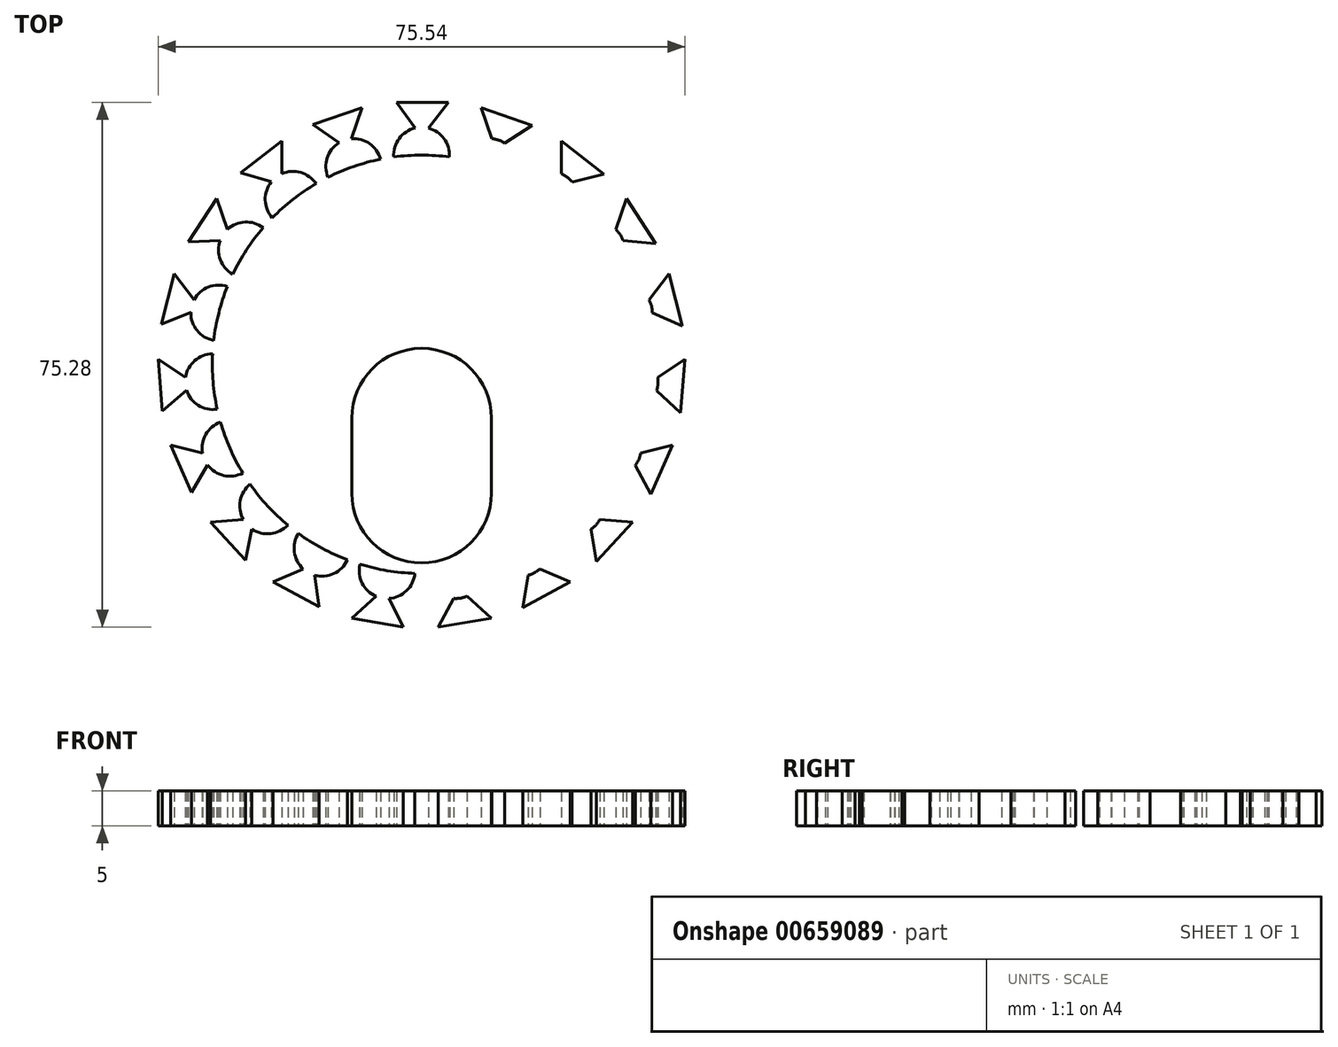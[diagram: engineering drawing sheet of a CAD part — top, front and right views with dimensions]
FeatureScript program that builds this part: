
annotation { "Feature Type Name" : "Feature", "Feature Type Description" : "" }
export const myFeature = defineFeature(function(context is Context, id is Id, definition is map)
    precondition{}
    {
        {
            var Q0;
            Q0=qCreatedBy(makeId("Top.planeOp"),FACE);
            var sketch = newSketch(context, id + "F0", { "sketchPlane" : qUnion([Q0])});
            skPoint(sketch, "E0.center", {"position": v(0, 0) * mm});
            skCircle(sketch, "E1", {"center": v(0, 0) * mm, "radius": 30 * mm});
            skArc(sketch, "E2", {"start": v(4, 29.73) * mm, "mid": v(0, 34) * mm, "end": v(-4, 29.73) * mm});
            skLineSegment(sketch, "E3", {"start": v(-0.9, 33.9) * mm, "end": v(-3.6, 37.58) * mm});
            skLineSegment(sketch, "E4", {"start": v(-3.6, 37.58) * mm, "end": v(3.87, 37.58) * mm});
            skLineSegment(sketch, "E5", {"start": v(3.87, 37.58) * mm, "end": v(0.96, 33.88) * mm});
            skPoint(sketch, "E6.orphan", {"position": v(0, 32.66) * mm});
            skLineSegment(sketch, "E7.1.0", {"start": v(-15.6, 34.37) * mm, "end": v(-8.55, 36.8) * mm});
            skLineSegment(sketch, "E7.1.1", {"start": v(-8.55, 36.8) * mm, "end": v(-10.1, 32.36) * mm});
            skLineSegment(sketch, "E7.1.2", {"start": v(-11.86, 31.77) * mm, "end": v(-15.6, 34.37) * mm});
            skArc(sketch, "E7.1.3", {"start": v(-5.88, 29.42) * mm, "mid": v(-11.04, 32.16) * mm, "end": v(-13.43, 26.83) * mm});
            skLineSegment(sketch, "E7.2.0", {"start": v(-25.92, 27.45) * mm, "end": v(-20.03, 32.03) * mm});
            skLineSegment(sketch, "E7.2.1", {"start": v(-20.03, 32.03) * mm, "end": v(-20.05, 27.33) * mm});
            skLineSegment(sketch, "E7.2.2", {"start": v(-21.53, 26.2) * mm, "end": v(-25.92, 27.45) * mm});
            skArc(sketch, "E7.2.3", {"start": v(-15.11, 25.92) * mm, "mid": v(-20.88, 26.83) * mm, "end": v(-21.41, 21.01) * mm});
            skLineSegment(sketch, "E7.3.0", {"start": v(-33.42, 17.54) * mm, "end": v(-29.34, 23.79) * mm});
            skLineSegment(sketch, "E7.3.1", {"start": v(-29.34, 23.79) * mm, "end": v(-27.84, 19.34) * mm});
            skLineSegment(sketch, "E7.3.2", {"start": v(-28.87, 17.78) * mm, "end": v(-33.42, 17.54) * mm});
            skArc(sketch, "E7.3.3", {"start": v(-22.7, 19.6) * mm, "mid": v(-28.46, 18.6) * mm, "end": v(-27.07, 12.92) * mm});
            skLineSegment(sketch, "E7.4.0", {"start": v(-37.3, 5.74) * mm, "end": v(-35.48, 12.97) * mm});
            skLineSegment(sketch, "E7.4.1", {"start": v(-35.48, 12.97) * mm, "end": v(-32.6, 9.25) * mm});
            skLineSegment(sketch, "E7.4.2", {"start": v(-33.08, 7.44) * mm, "end": v(-37.3, 5.74) * mm});
            skArc(sketch, "E7.4.3", {"start": v(-27.84, 11.17) * mm, "mid": v(-32.96, 8.35) * mm, "end": v(-29.8, 3.43) * mm});
            skLineSegment(sketch, "E7.5.0", {"start": v(-37.15, -6.68) * mm, "end": v(-37.77, 0.75) * mm});
            skLineSegment(sketch, "E7.5.1", {"start": v(-37.77, 0.75) * mm, "end": v(-33.85, -1.84) * mm});
            skLineSegment(sketch, "E7.5.2", {"start": v(-33.7, -3.7) * mm, "end": v(-37.15, -6.68) * mm});
            skArc(sketch, "E7.5.3", {"start": v(-29.96, 1.52) * mm, "mid": v(-33.88, -2.8) * mm, "end": v(-29.3, -6.43) * mm});
            skLineSegment(sketch, "E7.6.0", {"start": v(-32.97, -18.39) * mm, "end": v(-35.97, -11.55) * mm});
            skLineSegment(sketch, "E7.6.1", {"start": v(-35.97, -11.55) * mm, "end": v(-31.42, -12.73) * mm});
            skLineSegment(sketch, "E7.6.2", {"start": v(-30.68, -14.44) * mm, "end": v(-32.97, -18.39) * mm});
            skArc(sketch, "E7.6.3", {"start": v(-28.83, -8.29) * mm, "mid": v(-31.14, -13.66) * mm, "end": v(-25.63, -15.6) * mm});
            skLineSegment(sketch, "E7.7.0", {"start": v(-25.21, -28.1) * mm, "end": v(-30.26, -22.6) * mm});
            skLineSegment(sketch, "E7.7.1", {"start": v(-30.26, -22.6) * mm, "end": v(-25.58, -22.24) * mm});
            skLineSegment(sketch, "E7.7.2", {"start": v(-24.33, -23.62) * mm, "end": v(-25.21, -28.1) * mm});
            skArc(sketch, "E7.7.3", {"start": v(-24.58, -17.2) * mm, "mid": v(-25.01, -23.03) * mm, "end": v(-19.17, -23.07) * mm});
            skLineSegment(sketch, "E7.8.0", {"start": v(-14.72, -34.76) * mm, "end": v(-21.28, -31.2) * mm});
            skLineSegment(sketch, "E7.8.1", {"start": v(-21.28, -31.2) * mm, "end": v(-16.97, -29.34) * mm});
            skLineSegment(sketch, "E7.8.2", {"start": v(-15.34, -30.24) * mm, "end": v(-14.72, -34.76) * mm});
            skArc(sketch, "E7.8.3", {"start": v(-17.66, -24.25) * mm, "mid": v(-16.18, -29.9) * mm, "end": v(-10.64, -28.05) * mm});
            skLineSegment(sketch, "E7.9.0", {"start": v(-2.64, -37.66) * mm, "end": v(-10, -36.43) * mm});
            skLineSegment(sketch, "E7.9.1", {"start": v(-10, -36.43) * mm, "end": v(-6.53, -33.26) * mm});
            skLineSegment(sketch, "E7.9.2", {"start": v(-4.69, -33.58) * mm, "end": v(-2.64, -37.66) * mm});
            skArc(sketch, "E7.9.3", {"start": v(-8.83, -28.67) * mm, "mid": v(-5.6, -33.54) * mm, "end": v(-0.96, -29.98) * mm});
            skLineSegment(sketch, "E7.10.0", {"start": v(9.73, -36.47) * mm, "end": v(2.37, -37.7) * mm});
            skLineSegment(sketch, "E7.10.1", {"start": v(2.37, -37.7) * mm, "end": v(4.63, -33.58) * mm});
            skLineSegment(sketch, "E7.10.2", {"start": v(6.47, -33.29) * mm, "end": v(9.73, -36.47) * mm});
            skArc(sketch, "E7.10.3", {"start": v(0.96, -29.98) * mm, "mid": v(5.6, -33.54) * mm, "end": v(8.83, -28.67) * mm});
            skLineSegment(sketch, "E7.11.0", {"start": v(21.04, -31.34) * mm, "end": v(14.49, -34.89) * mm});
            skLineSegment(sketch, "E7.11.1", {"start": v(14.49, -34.89) * mm, "end": v(15.28, -30.26) * mm});
            skLineSegment(sketch, "E7.11.2", {"start": v(16.93, -29.38) * mm, "end": v(21.04, -31.34) * mm});
            skArc(sketch, "E7.11.3", {"start": v(10.64, -28.05) * mm, "mid": v(16.18, -29.9) * mm, "end": v(17.66, -24.25) * mm});
            skLineSegment(sketch, "E7.12.0", {"start": v(30.08, -22.8) * mm, "end": v(25.03, -28.3) * mm});
            skLineSegment(sketch, "E7.12.1", {"start": v(25.03, -28.3) * mm, "end": v(24.28, -23.66) * mm});
            skLineSegment(sketch, "E7.12.2", {"start": v(25.55, -22.3) * mm, "end": v(30.08, -22.8) * mm});
            skArc(sketch, "E7.12.3", {"start": v(19.17, -23.07) * mm, "mid": v(25.01, -23.03) * mm, "end": v(24.58, -17.2) * mm});
            skLineSegment(sketch, "E7.13.0", {"start": v(35.86, -11.8) * mm, "end": v(32.86, -18.63) * mm});
            skLineSegment(sketch, "E7.13.1", {"start": v(32.86, -18.63) * mm, "end": v(30.64, -14.5) * mm});
            skLineSegment(sketch, "E7.13.2", {"start": v(31.4, -12.79) * mm, "end": v(35.86, -11.8) * mm});
            skArc(sketch, "E7.13.3", {"start": v(25.63, -15.6) * mm, "mid": v(31.14, -13.66) * mm, "end": v(28.83, -8.29) * mm});
            skLineSegment(sketch, "E7.14.0", {"start": v(37.75, 0.48) * mm, "end": v(37.13, -6.96) * mm});
            skLineSegment(sketch, "E7.14.1", {"start": v(37.13, -6.96) * mm, "end": v(33.69, -3.76) * mm});
            skLineSegment(sketch, "E7.14.2", {"start": v(33.86, -1.9) * mm, "end": v(37.75, 0.48) * mm});
            skArc(sketch, "E7.14.3", {"start": v(29.3, -6.43) * mm, "mid": v(33.88, -2.8) * mm, "end": v(29.96, 1.52) * mm});
            skLineSegment(sketch, "E7.15.0", {"start": v(35.55, 12.7) * mm, "end": v(37.38, 5.48) * mm});
            skLineSegment(sketch, "E7.15.1", {"start": v(37.38, 5.48) * mm, "end": v(33.08, 7.38) * mm});
            skLineSegment(sketch, "E7.15.2", {"start": v(32.64, 9.2) * mm, "end": v(35.55, 12.7) * mm});
            skArc(sketch, "E7.15.3", {"start": v(29.8, 3.43) * mm, "mid": v(32.96, 8.35) * mm, "end": v(27.84, 11.17) * mm});
            skLineSegment(sketch, "E7.16.0", {"start": v(29.5, 23.56) * mm, "end": v(33.57, 17.32) * mm});
            skLineSegment(sketch, "E7.16.1", {"start": v(33.57, 17.32) * mm, "end": v(28.9, 17.73) * mm});
            skLineSegment(sketch, "E7.16.2", {"start": v(27.88, 19.3) * mm, "end": v(29.5, 23.56) * mm});
            skArc(sketch, "E7.16.3", {"start": v(27.07, 12.92) * mm, "mid": v(28.46, 18.6) * mm, "end": v(22.7, 19.6) * mm});
            skLineSegment(sketch, "E7.17.0", {"start": v(20.25, 31.86) * mm, "end": v(26.13, 27.28) * mm});
            skLineSegment(sketch, "E7.17.1", {"start": v(26.13, 27.28) * mm, "end": v(21.57, 26.15) * mm});
            skLineSegment(sketch, "E7.17.2", {"start": v(20.1, 27.3) * mm, "end": v(20.25, 31.86) * mm});
            skArc(sketch, "E7.17.3", {"start": v(21.41, 21.01) * mm, "mid": v(20.88, 26.83) * mm, "end": v(15.11, 25.92) * mm});
            skLineSegment(sketch, "E7.18.0", {"start": v(8.8, 36.7) * mm, "end": v(15.86, 34.29) * mm});
            skLineSegment(sketch, "E7.18.1", {"start": v(15.86, 34.29) * mm, "end": v(11.91, 31.73) * mm});
            skLineSegment(sketch, "E7.18.2", {"start": v(10.15, 32.35) * mm, "end": v(8.8, 36.7) * mm});
            skArc(sketch, "E7.18.3", {"start": v(13.43, 26.83) * mm, "mid": v(11.04, 32.16) * mm, "end": v(5.88, 29.42) * mm});
            skArc(sketch, "E8.0.startCap", {"start": v(-10, -7.7) * mm, "mid": v(0, 2.3) * mm, "end": v(10, -7.7) * mm});
            skArc(sketch, "E8.0.endCap", {"start": v(10, -18.5) * mm, "mid": v(0, -28.5) * mm, "end": v(-10, -18.5) * mm});
            skLineSegment(sketch, "E8.0.left", {"start": v(10, -7.7) * mm, "end": v(10, -18.5) * mm});
            skLineSegment(sketch, "E8.0.right", {"start": v(-10, -7.7) * mm, "end": v(-10, -18.5) * mm});
            skCircle(sketch, "E9", {"center": v(-15.8, 9.6) * mm, "radius": 7.2 * mm});
            skCircle(sketch, "E10", {"center": v(0, 19.07) * mm, "radius": 6.01 * mm});
            skLineSegment(sketch, "E11.MirrorCS", {"start": v(21.28, -31.2) * mm, "end": v(16.97, -29.34) * mm});
            skLineSegment(sketch, "E12.MirrorCS", {"start": v(35.48, 12.97) * mm, "end": v(32.6, 9.25) * mm});
            skArc(sketch, "E13.MirrorCS", {"start": v(22.7, 19.6) * mm, "mid": v(28.46, 18.6) * mm, "end": v(27.07, 12.92) * mm});
            skLineSegment(sketch, "E14.MirrorCS", {"start": v(33.7, -3.7) * mm, "end": v(37.15, -6.68) * mm});
            skLineSegment(sketch, "E15.MirrorCS", {"start": v(4.69, -33.58) * mm, "end": v(2.64, -37.66) * mm});
            skArc(sketch, "E16.MirrorCS", {"start": v(15.11, 25.92) * mm, "mid": v(20.88, 26.83) * mm, "end": v(21.41, 21.01) * mm});
            skLineSegment(sketch, "E17.MirrorCS", {"start": v(21.53, 26.2) * mm, "end": v(25.92, 27.45) * mm});
            skLineSegment(sketch, "E18.MirrorCS", {"start": v(20.03, 32.03) * mm, "end": v(20.05, 27.33) * mm});
            skLineSegment(sketch, "E19.MirrorCS", {"start": v(11.86, 31.77) * mm, "end": v(15.6, 34.37) * mm});
            skLineSegment(sketch, "E20.MirrorCS", {"start": v(8.55, 36.8) * mm, "end": v(10.1, 32.36) * mm});
            skLineSegment(sketch, "E21.MirrorCS", {"start": v(0.9, 33.9) * mm, "end": v(3.6, 37.58) * mm});
            skLineSegment(sketch, "E22.MirrorCS", {"start": v(28.87, 17.78) * mm, "end": v(33.42, 17.54) * mm});
            skLineSegment(sketch, "E23.MirrorCS", {"start": v(29.34, 23.79) * mm, "end": v(27.84, 19.34) * mm});
            skLineSegment(sketch, "E24.MirrorCS", {"start": v(10, -36.43) * mm, "end": v(6.53, -33.26) * mm});
            skLineSegment(sketch, "E25.MirrorCS", {"start": v(24.33, -23.62) * mm, "end": v(25.21, -28.1) * mm});
            skLineSegment(sketch, "E26.MirrorCS", {"start": v(37.77, 0.75) * mm, "end": v(33.85, -1.84) * mm});
            skLineSegment(sketch, "E27.MirrorCS", {"start": v(30.26, -22.6) * mm, "end": v(25.58, -22.24) * mm});
            skArc(sketch, "E28.MirrorCS", {"start": v(28.83, -8.29) * mm, "mid": v(31.14, -13.66) * mm, "end": v(25.63, -15.6) * mm});
            skArc(sketch, "E29.MirrorCS", {"start": v(17.66, -24.25) * mm, "mid": v(16.18, -29.9) * mm, "end": v(10.64, -28.05) * mm});
            skLineSegment(sketch, "E30.MirrorCS", {"start": v(30.68, -14.44) * mm, "end": v(32.97, -18.39) * mm});
            skLineSegment(sketch, "E31.MirrorCS", {"start": v(15.34, -30.24) * mm, "end": v(14.72, -34.76) * mm});
            skLineSegment(sketch, "E32.MirrorCS", {"start": v(35.97, -11.55) * mm, "end": v(31.42, -12.73) * mm});
            skLineSegment(sketch, "E33.MirrorCS", {"start": v(33.08, 7.44) * mm, "end": v(37.3, 5.74) * mm});
            skLineSegment(sketch, "E34.MirrorCS", {"start": v(14.72, -34.76) * mm, "end": v(21.28, -31.2) * mm});
            skLineSegment(sketch, "E35.MirrorCS", {"start": v(37.3, 5.74) * mm, "end": v(35.48, 12.97) * mm});
            skArc(sketch, "E36.MirrorCS", {"start": v(29.96, 1.52) * mm, "mid": v(33.88, -2.8) * mm, "end": v(29.3, -6.43) * mm});
            skArc(sketch, "E37.MirrorCS", {"start": v(24.58, -17.2) * mm, "mid": v(25.01, -23.03) * mm, "end": v(19.17, -23.07) * mm});
            skArc(sketch, "E38.MirrorCS", {"start": v(8.83, -28.67) * mm, "mid": v(5.6, -33.54) * mm, "end": v(0.96, -29.98) * mm});
            skLineSegment(sketch, "E39.MirrorCS", {"start": v(25.92, 27.45) * mm, "end": v(20.03, 32.03) * mm});
            skArc(sketch, "E40.MirrorCS", {"start": v(5.88, 29.42) * mm, "mid": v(11.04, 32.16) * mm, "end": v(13.43, 26.83) * mm});
            skLineSegment(sketch, "E41.MirrorCS", {"start": v(15.6, 34.37) * mm, "end": v(8.55, 36.8) * mm});
            skLineSegment(sketch, "E42.MirrorCS", {"start": v(33.42, 17.54) * mm, "end": v(29.34, 23.79) * mm});
            skCircle(sketch, "E43.MirrorC", {"center": v(15.8, 9.6) * mm, "radius": 7.2 * mm});
            skLineSegment(sketch, "E44.MirrorCS", {"start": v(2.64, -37.66) * mm, "end": v(10, -36.43) * mm});
            skLineSegment(sketch, "E45.MirrorCS", {"start": v(37.15, -6.68) * mm, "end": v(37.77, 0.75) * mm});
            skLineSegment(sketch, "E46.MirrorCS", {"start": v(25.21, -28.1) * mm, "end": v(30.26, -22.6) * mm});
            skLineSegment(sketch, "E47.MirrorCS", {"start": v(32.97, -18.39) * mm, "end": v(35.97, -11.55) * mm});
            skArc(sketch, "E48.MirrorCS", {"start": v(27.84, 11.17) * mm, "mid": v(32.96, 8.35) * mm, "end": v(29.8, 3.43) * mm});
            skLineSegment(sketch, "E49.trimOffspring", {"start": v(0, 34) * mm, "end": v(0, 30) * mm});
            skPoint(sketch, "E50.start.orphan", {"position": v(0, 50.63) * mm});
            skLineSegment(sketch, "E51.trimOffspring", {"start": v(0, 2.3) * mm, "end": v(0, 0) * mm});
            skSolve(sketch);
        }
        {
            var Q0;
            {var subQ0=sQuery(id+"F0.wireOp",EDGE,"E7.14.2");Q0=makeQuery(id+"F0.imprint","IMPRINT",FACE,{"disambiguationData":[TD([[makeQuery(id+"F0.imprint","IMPRINT",EDGE,{"derivedFrom":subQ0}),-1.0]])]});}
            var Q1;
            Q1=makeQuery(id+"F0.imprint","IMPRINT",FACE,{"disambiguationData":[TD([[makeQuery(id+"F0.imprint","IMPRINT",EDGE,{"derivedFrom":sQuery(id+"F0.wireOp",EDGE,"E7.7.0")}),-1.0]])]});
            var Q2;
            Q2=makeQuery(id+"F0.imprint","IMPRINT",FACE,{"disambiguationData":[TD([[makeQuery(id+"F0.imprint","IMPRINT",EDGE,{"derivedFrom":sQuery(id+"F0.wireOp",EDGE,"E7.6.0")}),-1.0]])]});
            var Q3;
            Q3=makeQuery(id+"F0.imprint","IMPRINT",FACE,{"disambiguationData":[TD([[makeQuery(id+"F0.imprint","IMPRINT",EDGE,{"derivedFrom":sQuery(id+"F0.wireOp",EDGE,"E7.5.0")}),-1.0]])]});
            var Q4;
            {var subQ0=sQuery(id+"F0.wireOp",EDGE,"E7.17.2");Q4=makeQuery(id+"F0.imprint","IMPRINT",FACE,{"disambiguationData":[TD([[makeQuery(id+"F0.imprint","IMPRINT",EDGE,{"derivedFrom":subQ0}),-1.0]])]});}
            var Q5;
            Q5=makeQuery(id+"F0.imprint","IMPRINT",FACE,{"disambiguationData":[TD([[makeQuery(id+"F0.imprint","IMPRINT",EDGE,{"derivedFrom":sQuery(id+"F0.wireOp",EDGE,"E7.4.0")}),-1.0]])]});
            var Q6;
            Q6=makeQuery(id+"F0.imprint","IMPRINT",FACE,{"disambiguationData":[TD([[makeQuery(id+"F0.imprint","IMPRINT",EDGE,{"derivedFrom":sQuery(id+"F0.wireOp",EDGE,"E7.2.0")}),-1.0]])]});
            var Q7;
            {var subQ0=sQuery(id+"F0.wireOp",EDGE,"E7.16.2");Q7=makeQuery(id+"F0.imprint","IMPRINT",FACE,{"disambiguationData":[TD([[makeQuery(id+"F0.imprint","IMPRINT",EDGE,{"derivedFrom":subQ0}),-1.0]])]});}
            var Q8;
            {var subQ0=sQuery(id+"F0.wireOp",EDGE,"E7.11.2");Q8=makeQuery(id+"F0.imprint","IMPRINT",FACE,{"disambiguationData":[TD([[makeQuery(id+"F0.imprint","IMPRINT",EDGE,{"derivedFrom":subQ0}),-1.0]])]});}
            var Q9;
            Q9=makeQuery(id+"F0.imprint","IMPRINT",FACE,{"disambiguationData":[TD([[makeQuery(id+"F0.imprint","IMPRINT",EDGE,{"derivedFrom":sQuery(id+"F0.wireOp",EDGE,"E8.0.endCap")}),1.0]])]});
            var Q10;
            {var subQ3=sQuery(id+"F0.wireOp",EDGE,"E49.trimOffspring");Q10=makeQuery(id+"F0.imprint","IMPRINT",FACE,{"disambiguationData":[TD([[makeQuery(id+"F0.imprint","IMPRINT",EDGE,{"derivedFrom":subQ3}),-1.0]])]});}
            var Q11;
            {var subQ0=sQuery(id+"F0.wireOp",EDGE,"E7.9.3");var subQ1=sQuery(id+"F0.wireOp",EDGE,"E1");var subQ2=makeQuery(id+"F0.imprint","INTERSECT",VERTEX,{"disambiguationData":[OD(0.0)],"derivedFrom":[subQ1,subQ0]});Q11=makeQuery(id+"F0.imprint","IMPRINT",FACE,{"disambiguationData":[TD([[makeQuery(id+"F0.imprint","IMPRINT",EDGE,{"disambiguationData":[TD([[subQ2,-1.0]])],"derivedFrom":subQ1}),-1.0]])]});}
            var Q12;
            {var subQ2=sQuery(id+"F0.wireOp",EDGE,"E49.trimOffspring");Q12=makeQuery(id+"F0.imprint","IMPRINT",FACE,{"disambiguationData":[TD([[makeQuery(id+"F0.imprint","IMPRINT",EDGE,{"derivedFrom":subQ2}),1.0]])]});}
            var Q13;
            {var subQ0=sQuery(id+"F0.wireOp",EDGE,"E7.8.3");var subQ1=sQuery(id+"F0.wireOp",EDGE,"E1");var subQ2=makeQuery(id+"F0.imprint","INTERSECT",VERTEX,{"disambiguationData":[OD(0.0)],"derivedFrom":[subQ1,subQ0]});Q13=makeQuery(id+"F0.imprint","IMPRINT",FACE,{"disambiguationData":[TD([[makeQuery(id+"F0.imprint","IMPRINT",EDGE,{"disambiguationData":[TD([[subQ2,-1.0]])],"derivedFrom":subQ1}),-1.0]])]});}
            var Q14;
            {var subQ0=sQuery(id+"F0.wireOp",EDGE,"E7.7.3");var subQ1=sQuery(id+"F0.wireOp",EDGE,"E1");var subQ2=makeQuery(id+"F0.imprint","INTERSECT",VERTEX,{"disambiguationData":[OD(0.0)],"derivedFrom":[subQ1,subQ0]});Q14=makeQuery(id+"F0.imprint","IMPRINT",FACE,{"disambiguationData":[TD([[makeQuery(id+"F0.imprint","IMPRINT",EDGE,{"disambiguationData":[TD([[subQ2,-1.0]])],"derivedFrom":subQ1}),-1.0]])]});}
            var Q15;
            Q15=makeQuery(id+"F0.imprint","IMPRINT",FACE,{"disambiguationData":[TD([[makeQuery(id+"F0.imprint","IMPRINT",EDGE,{"derivedFrom":sQuery(id+"F0.wireOp",EDGE,"E7.9.0")}),-1.0]])]});
            var Q16;
            Q16=makeQuery(id+"F0.imprint","IMPRINT",FACE,{"disambiguationData":[TD([[makeQuery(id+"F0.imprint","IMPRINT",EDGE,{"derivedFrom":sQuery(id+"F0.wireOp",EDGE,"E7.8.0")}),-1.0]])]});
            var Q17;
            {var subQ0=sQuery(id+"F0.wireOp",EDGE,"E7.6.3");var subQ1=sQuery(id+"F0.wireOp",EDGE,"E1");var subQ2=makeQuery(id+"F0.imprint","INTERSECT",VERTEX,{"disambiguationData":[OD(0.0)],"derivedFrom":[subQ1,subQ0]});Q17=makeQuery(id+"F0.imprint","IMPRINT",FACE,{"disambiguationData":[TD([[makeQuery(id+"F0.imprint","IMPRINT",EDGE,{"disambiguationData":[TD([[subQ2,-1.0]])],"derivedFrom":subQ1}),-1.0]])]});}
            var Q18;
            Q18=makeQuery(id+"F0.imprint","IMPRINT",FACE,{"disambiguationData":[TD([[makeQuery(id+"F0.imprint","IMPRINT",EDGE,{"derivedFrom":sQuery(id+"F0.wireOp",EDGE,"E7.3.0")}),-1.0]])]});
            var Q19;
            Q19=makeQuery(id+"F0.imprint","IMPRINT",FACE,{"disambiguationData":[TD([[makeQuery(id+"F0.imprint","IMPRINT",EDGE,{"derivedFrom":sQuery(id+"F0.wireOp",EDGE,"E7.1.0")}),-1.0]])]});
            var Q20;
            {var subQ0=sQuery(id+"F0.wireOp",EDGE,"E7.2.3");var subQ1=sQuery(id+"F0.wireOp",EDGE,"E1");var subQ2=makeQuery(id+"F0.imprint","INTERSECT",VERTEX,{"disambiguationData":[OD(0.0)],"derivedFrom":[subQ1,subQ0]});Q20=makeQuery(id+"F0.imprint","IMPRINT",FACE,{"disambiguationData":[TD([[makeQuery(id+"F0.imprint","IMPRINT",EDGE,{"disambiguationData":[TD([[subQ2,-1.0]])],"derivedFrom":subQ1}),-1.0]])]});}
            var Q21;
            {var subQ0=sQuery(id+"F0.wireOp",EDGE,"E7.1.3");var subQ1=sQuery(id+"F0.wireOp",EDGE,"E1");var subQ2=makeQuery(id+"F0.imprint","INTERSECT",VERTEX,{"disambiguationData":[OD(0.0)],"derivedFrom":[subQ1,subQ0]});Q21=makeQuery(id+"F0.imprint","IMPRINT",FACE,{"disambiguationData":[TD([[makeQuery(id+"F0.imprint","IMPRINT",EDGE,{"disambiguationData":[TD([[subQ2,-1.0]])],"derivedFrom":subQ1}),-1.0]])]});}
            var Q22;
            {var subQ0=sQuery(id+"F0.wireOp",EDGE,"E7.5.3");var subQ1=sQuery(id+"F0.wireOp",EDGE,"E1");var subQ2=makeQuery(id+"F0.imprint","INTERSECT",VERTEX,{"disambiguationData":[OD(0.0)],"derivedFrom":[subQ1,subQ0]});Q22=makeQuery(id+"F0.imprint","IMPRINT",FACE,{"disambiguationData":[TD([[makeQuery(id+"F0.imprint","IMPRINT",EDGE,{"disambiguationData":[TD([[subQ2,-1.0]])],"derivedFrom":subQ1}),-1.0]])]});}
            var Q23;
            {var subQ0=sQuery(id+"F0.wireOp",EDGE,"E7.3.3");var subQ1=sQuery(id+"F0.wireOp",EDGE,"E1");var subQ2=makeQuery(id+"F0.imprint","INTERSECT",VERTEX,{"disambiguationData":[OD(0.0)],"derivedFrom":[subQ1,subQ0]});Q23=makeQuery(id+"F0.imprint","IMPRINT",FACE,{"disambiguationData":[TD([[makeQuery(id+"F0.imprint","IMPRINT",EDGE,{"disambiguationData":[TD([[subQ2,-1.0]])],"derivedFrom":subQ1}),-1.0]])]});}
            var Q24;
            {var subQ0=sQuery(id+"F0.wireOp",EDGE,"E7.4.3");var subQ1=sQuery(id+"F0.wireOp",EDGE,"E1");var subQ2=makeQuery(id+"F0.imprint","INTERSECT",VERTEX,{"disambiguationData":[OD(0.0)],"derivedFrom":[subQ1,subQ0]});Q24=makeQuery(id+"F0.imprint","IMPRINT",FACE,{"disambiguationData":[TD([[makeQuery(id+"F0.imprint","IMPRINT",EDGE,{"disambiguationData":[TD([[subQ2,-1.0]])],"derivedFrom":subQ1}),-1.0]])]});}
            var Q25;
            {var subQ0=sQuery(id+"F0.wireOp",EDGE,"E7.12.2");Q25=makeQuery(id+"F0.imprint","IMPRINT",FACE,{"disambiguationData":[TD([[makeQuery(id+"F0.imprint","IMPRINT",EDGE,{"derivedFrom":subQ0}),-1.0]])]});}
            var Q26;
            {var subQ1=sQuery(id+"F0.wireOp",EDGE,"E3");Q26=makeQuery(id+"F0.imprint","IMPRINT",FACE,{"disambiguationData":[TD([[makeQuery(id+"F0.imprint","IMPRINT",EDGE,{"derivedFrom":subQ1}),-1.0]])]});}
            var Q27;
            {var subQ0=sQuery(id+"F0.wireOp",EDGE,"E38.MirrorCS");var subQ3=sQuery(id+"F0.wireOp",EDGE,"E1");var subQ4=makeQuery(id+"F0.imprint","INTERSECT",VERTEX,{"disambiguationData":[OD(0.0)],"derivedFrom":[subQ3,subQ0]});Q27=makeQuery(id+"F0.imprint","IMPRINT",FACE,{"disambiguationData":[TD([[makeQuery(id+"F0.imprint","IMPRINT",EDGE,{"disambiguationData":[TD([[subQ4,1.0]])],"derivedFrom":subQ3}),-1.0]])]});}
            var Q28;
            {var subQ0=sQuery(id+"F0.wireOp",EDGE,"E13.MirrorCS");var subQ3=sQuery(id+"F0.wireOp",EDGE,"E1");var subQ4=makeQuery(id+"F0.imprint","INTERSECT",VERTEX,{"disambiguationData":[OD(0.0)],"derivedFrom":[subQ3,subQ0]});Q28=makeQuery(id+"F0.imprint","IMPRINT",FACE,{"disambiguationData":[TD([[makeQuery(id+"F0.imprint","IMPRINT",EDGE,{"disambiguationData":[TD([[subQ4,1.0]])],"derivedFrom":subQ3}),-1.0]])]});}
            var Q29;
            {var subQ0=sQuery(id+"F0.wireOp",EDGE,"E48.MirrorCS");var subQ3=sQuery(id+"F0.wireOp",EDGE,"E1");var subQ4=makeQuery(id+"F0.imprint","INTERSECT",VERTEX,{"disambiguationData":[OD(0.0)],"derivedFrom":[subQ3,subQ0]});Q29=makeQuery(id+"F0.imprint","IMPRINT",FACE,{"disambiguationData":[TD([[makeQuery(id+"F0.imprint","IMPRINT",EDGE,{"disambiguationData":[TD([[subQ4,1.0]])],"derivedFrom":subQ3}),-1.0]])]});}
            var Q30;
            {var subQ0=sQuery(id+"F0.wireOp",EDGE,"E40.MirrorCS");var subQ3=sQuery(id+"F0.wireOp",EDGE,"E1");var subQ4=makeQuery(id+"F0.imprint","INTERSECT",VERTEX,{"disambiguationData":[OD(0.0)],"derivedFrom":[subQ3,subQ0]});Q30=makeQuery(id+"F0.imprint","IMPRINT",FACE,{"disambiguationData":[TD([[makeQuery(id+"F0.imprint","IMPRINT",EDGE,{"disambiguationData":[TD([[subQ4,1.0]])],"derivedFrom":subQ3}),-1.0]])]});}
            var Q31;
            {var subQ0=sQuery(id+"F0.wireOp",EDGE,"E7.18.2");Q31=makeQuery(id+"F0.imprint","IMPRINT",FACE,{"disambiguationData":[TD([[makeQuery(id+"F0.imprint","IMPRINT",EDGE,{"derivedFrom":subQ0}),-1.0]])]});}
            var Q32;
            {var subQ0=sQuery(id+"F0.wireOp",EDGE,"E7.15.2");Q32=makeQuery(id+"F0.imprint","IMPRINT",FACE,{"disambiguationData":[TD([[makeQuery(id+"F0.imprint","IMPRINT",EDGE,{"derivedFrom":subQ0}),-1.0]])]});}
            var Q33;
            {var subQ0=sQuery(id+"F0.wireOp",EDGE,"E16.MirrorCS");var subQ3=sQuery(id+"F0.wireOp",EDGE,"E1");var subQ4=makeQuery(id+"F0.imprint","INTERSECT",VERTEX,{"disambiguationData":[OD(0.0)],"derivedFrom":[subQ3,subQ0]});Q33=makeQuery(id+"F0.imprint","IMPRINT",FACE,{"disambiguationData":[TD([[makeQuery(id+"F0.imprint","IMPRINT",EDGE,{"disambiguationData":[TD([[subQ4,1.0]])],"derivedFrom":subQ3}),-1.0]])]});}
            var Q34;
            {var subQ0=sQuery(id+"F0.wireOp",EDGE,"E28.MirrorCS");var subQ3=sQuery(id+"F0.wireOp",EDGE,"E1");var subQ4=makeQuery(id+"F0.imprint","INTERSECT",VERTEX,{"disambiguationData":[OD(0.0)],"derivedFrom":[subQ3,subQ0]});Q34=makeQuery(id+"F0.imprint","IMPRINT",FACE,{"disambiguationData":[TD([[makeQuery(id+"F0.imprint","IMPRINT",EDGE,{"disambiguationData":[TD([[subQ4,1.0]])],"derivedFrom":subQ3}),-1.0]])]});}
            var Q35;
            {var subQ0=sQuery(id+"F0.wireOp",EDGE,"E7.13.2");Q35=makeQuery(id+"F0.imprint","IMPRINT",FACE,{"disambiguationData":[TD([[makeQuery(id+"F0.imprint","IMPRINT",EDGE,{"derivedFrom":subQ0}),-1.0]])]});}
            var Q36;
            {var subQ0=sQuery(id+"F0.wireOp",EDGE,"E7.10.2");Q36=makeQuery(id+"F0.imprint","IMPRINT",FACE,{"disambiguationData":[TD([[makeQuery(id+"F0.imprint","IMPRINT",EDGE,{"derivedFrom":subQ0}),-1.0]])]});}
            var Q37;
            {var subQ0=sQuery(id+"F0.wireOp",EDGE,"E37.MirrorCS");var subQ4=sQuery(id+"F0.wireOp",EDGE,"E1");var subQ5=makeQuery(id+"F0.imprint","INTERSECT",VERTEX,{"disambiguationData":[OD(0.0)],"derivedFrom":[subQ4,subQ0]});Q37=makeQuery(id+"F0.imprint","IMPRINT",FACE,{"disambiguationData":[TD([[makeQuery(id+"F0.imprint","IMPRINT",EDGE,{"disambiguationData":[TD([[subQ5,1.0]])],"derivedFrom":subQ4}),-1.0]])]});}
            var Q38;
            {var subQ0=sQuery(id+"F0.wireOp",EDGE,"E36.MirrorCS");var subQ4=sQuery(id+"F0.wireOp",EDGE,"E1");var subQ5=makeQuery(id+"F0.imprint","INTERSECT",VERTEX,{"disambiguationData":[OD(0.0)],"derivedFrom":[subQ4,subQ0]});Q38=makeQuery(id+"F0.imprint","IMPRINT",FACE,{"disambiguationData":[TD([[makeQuery(id+"F0.imprint","IMPRINT",EDGE,{"disambiguationData":[TD([[subQ5,1.0]])],"derivedFrom":subQ4}),-1.0]])]});}
            var Q39;
            {var subQ0=sQuery(id+"F0.wireOp",EDGE,"E29.MirrorCS");var subQ3=sQuery(id+"F0.wireOp",EDGE,"E1");var subQ4=makeQuery(id+"F0.imprint","INTERSECT",VERTEX,{"disambiguationData":[OD(0.0)],"derivedFrom":[subQ3,subQ0]});Q39=makeQuery(id+"F0.imprint","IMPRINT",FACE,{"disambiguationData":[TD([[makeQuery(id+"F0.imprint","IMPRINT",EDGE,{"disambiguationData":[TD([[subQ4,1.0]])],"derivedFrom":subQ3}),-1.0]])]});}
            var Q40;
            Q40=makeQuery(id+"F0.imprint","IMPRINT",FACE,{"disambiguationData":[TD([[makeQuery(id+"F0.imprint","IMPRINT",EDGE,{"derivedFrom":sQuery(id+"F0.wireOp",EDGE,"E7.11.0")}),-1.0]])]});
            var Q41;
            {var subQ0=sQuery(id+"F0.wireOp",EDGE,"E7.18.2");Q41=makeQuery(id+"F0.imprint","IMPRINT",FACE,{"disambiguationData":[TD([[makeQuery(id+"F0.imprint","IMPRINT",EDGE,{"derivedFrom":subQ0}),1.0]])]});}
            var Q42;
            Q42=makeQuery(id+"F0.imprint","IMPRINT",FACE,{"disambiguationData":[TD([[makeQuery(id+"F0.imprint","IMPRINT",EDGE,{"derivedFrom":sQuery(id+"F0.wireOp",EDGE,"E7.18.0")}),-1.0]])]});
            var Q43;
            {var subQ0=sQuery(id+"F0.wireOp",EDGE,"E7.17.2");Q43=makeQuery(id+"F0.imprint","IMPRINT",FACE,{"disambiguationData":[TD([[makeQuery(id+"F0.imprint","IMPRINT",EDGE,{"derivedFrom":subQ0}),1.0]])]});}
            var Q44;
            Q44=makeQuery(id+"F0.imprint","IMPRINT",FACE,{"disambiguationData":[TD([[makeQuery(id+"F0.imprint","IMPRINT",EDGE,{"derivedFrom":sQuery(id+"F0.wireOp",EDGE,"E7.12.0")}),-1.0]])]});
            var Q45;
            Q45=makeQuery(id+"F0.imprint","IMPRINT",FACE,{"disambiguationData":[TD([[makeQuery(id+"F0.imprint","IMPRINT",EDGE,{"derivedFrom":sQuery(id+"F0.wireOp",EDGE,"E7.14.0")}),-1.0]])]});
            var Q46;
            Q46=makeQuery(id+"F0.imprint","IMPRINT",FACE,{"disambiguationData":[TD([[makeQuery(id+"F0.imprint","IMPRINT",EDGE,{"derivedFrom":sQuery(id+"F0.wireOp",EDGE,"E7.17.0")}),-1.0]])]});
            var Q47;
            {var subQ0=sQuery(id+"F0.wireOp",EDGE,"E7.10.2");Q47=makeQuery(id+"F0.imprint","IMPRINT",FACE,{"disambiguationData":[TD([[makeQuery(id+"F0.imprint","IMPRINT",EDGE,{"derivedFrom":subQ0}),1.0]])]});}
            var Q48;
            {var subQ0=sQuery(id+"F0.wireOp",EDGE,"E7.16.2");Q48=makeQuery(id+"F0.imprint","IMPRINT",FACE,{"disambiguationData":[TD([[makeQuery(id+"F0.imprint","IMPRINT",EDGE,{"derivedFrom":subQ0}),1.0]])]});}
            var Q49;
            Q49=makeQuery(id+"F0.imprint","IMPRINT",FACE,{"disambiguationData":[TD([[makeQuery(id+"F0.imprint","IMPRINT",EDGE,{"derivedFrom":sQuery(id+"F0.wireOp",EDGE,"E7.10.0")}),-1.0]])]});
            var Q50;
            Q50=makeQuery(id+"F0.imprint","IMPRINT",FACE,{"disambiguationData":[TD([[makeQuery(id+"F0.imprint","IMPRINT",EDGE,{"derivedFrom":sQuery(id+"F0.wireOp",EDGE,"E7.16.0")}),-1.0]])]});
            var Q51;
            {var subQ0=sQuery(id+"F0.wireOp",EDGE,"E7.15.2");Q51=makeQuery(id+"F0.imprint","IMPRINT",FACE,{"disambiguationData":[TD([[makeQuery(id+"F0.imprint","IMPRINT",EDGE,{"derivedFrom":subQ0}),1.0]])]});}
            var Q52;
            Q52=makeQuery(id+"F0.imprint","IMPRINT",FACE,{"disambiguationData":[TD([[makeQuery(id+"F0.imprint","IMPRINT",EDGE,{"derivedFrom":sQuery(id+"F0.wireOp",EDGE,"E7.15.0")}),-1.0]])]});
            var Q53;
            {var subQ0=sQuery(id+"F0.wireOp",EDGE,"E7.14.2");Q53=makeQuery(id+"F0.imprint","IMPRINT",FACE,{"disambiguationData":[TD([[makeQuery(id+"F0.imprint","IMPRINT",EDGE,{"derivedFrom":subQ0}),1.0]])]});}
            var Q54;
            {var subQ0=sQuery(id+"F0.wireOp",EDGE,"E5");Q54=makeQuery(id+"F0.imprint","IMPRINT",FACE,{"disambiguationData":[TD([[makeQuery(id+"F0.imprint","IMPRINT",EDGE,{"derivedFrom":subQ0}),-1.0]])]});}
            var Q55;
            {var subQ0=sQuery(id+"F0.wireOp",EDGE,"E7.12.2");Q55=makeQuery(id+"F0.imprint","IMPRINT",FACE,{"disambiguationData":[TD([[makeQuery(id+"F0.imprint","IMPRINT",EDGE,{"derivedFrom":subQ0}),1.0]])]});}
            var Q56;
            {var subQ0=sQuery(id+"F0.wireOp",EDGE,"E7.13.2");Q56=makeQuery(id+"F0.imprint","IMPRINT",FACE,{"disambiguationData":[TD([[makeQuery(id+"F0.imprint","IMPRINT",EDGE,{"derivedFrom":subQ0}),1.0]])]});}
            var Q57;
            Q57=makeQuery(id+"F0.imprint","IMPRINT",FACE,{"disambiguationData":[TD([[makeQuery(id+"F0.imprint","IMPRINT",EDGE,{"derivedFrom":sQuery(id+"F0.wireOp",EDGE,"E7.13.0")}),-1.0]])]});
            var Q58;
            {var subQ0=sQuery(id+"F0.wireOp",EDGE,"E7.11.2");Q58=makeQuery(id+"F0.imprint","IMPRINT",FACE,{"disambiguationData":[TD([[makeQuery(id+"F0.imprint","IMPRINT",EDGE,{"derivedFrom":subQ0}),1.0]])]});}
            extrude(context, id + "F1", {"entities" : qUnion([Q0, Q1, Q2, Q3, Q4, Q5, Q6, Q7, Q8, Q9, Q10, Q11, Q12, Q13, Q14, Q15, Q16, Q17, Q18, Q19, Q20, Q21, Q22, Q23, Q24, Q25, Q26, Q27, Q28, Q29, Q30, Q31, Q32, Q33, Q34, Q35, Q36, Q37, Q38, Q39, Q40, Q41, Q42, Q43, Q44, Q45, Q46, Q47, Q48, Q49, Q50, Q51, Q52, Q53, Q54, Q55, Q56, Q57, Q58]), "depth" : 5 * mm, "offsetDistance" : 25 * mm});
        }
    });
